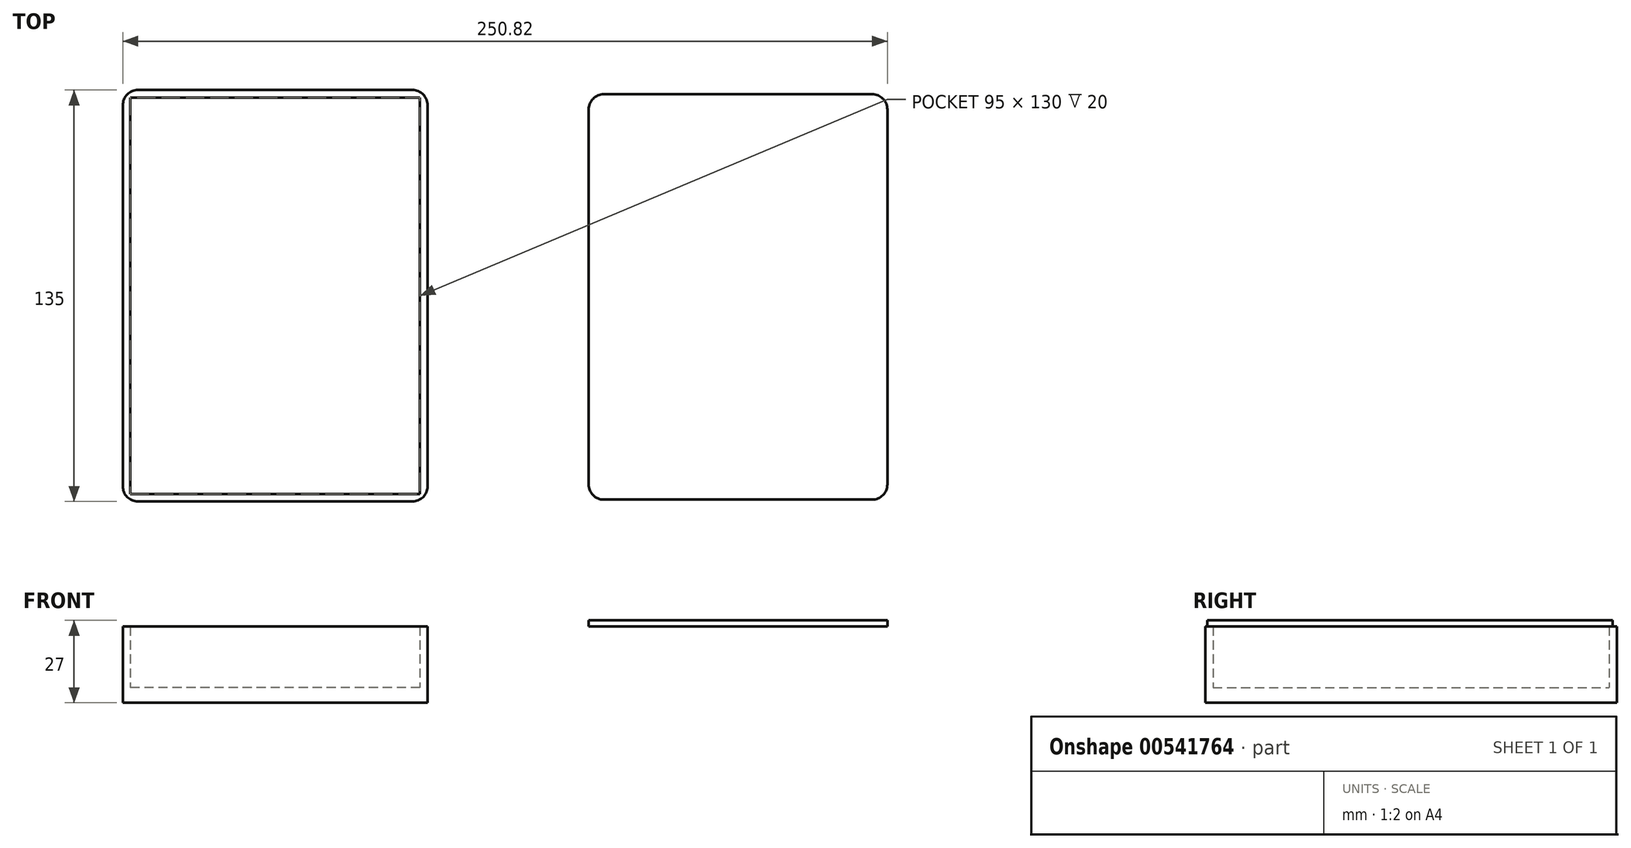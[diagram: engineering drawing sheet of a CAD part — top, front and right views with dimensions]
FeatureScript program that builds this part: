
annotation { "Feature Type Name" : "Feature", "Feature Type Description" : "" }
export const myFeature = defineFeature(function(context is Context, id is Id, definition is map)
    precondition{}
    {
        {
            var Q0;
            Q0=qCreatedBy(makeId("Top.planeOp"),FACE);
            var sketch = newSketch(context, id + "F0", { "sketchPlane" : qUnion([Q0])});
            skLineSegment(sketch, "E0.bottom", {"start": v(-50, -67.5) * mm, "end": v(50, -67.5) * mm});
            skLineSegment(sketch, "E0.top", {"start": v(-50, 67.5) * mm, "end": v(50, 67.5) * mm});
            skLineSegment(sketch, "E0.left", {"start": v(-50, -67.5) * mm, "end": v(-50, 67.5) * mm});
            skLineSegment(sketch, "E0.right", {"start": v(50, -67.5) * mm, "end": v(50, 67.5) * mm});
            skPoint(sketch, "E0.middle", {"position": v(0, 0) * mm});
            skSolve(sketch);
        }
        {
            var Q0;
            Q0=makeQuery(id+"F0.imprint","IMPRINT",FACE,{"disambiguationData":[TD([[makeQuery(id+"F0.imprint","IMPRINT",EDGE,{"derivedFrom":sQuery(id+"F0.wireOp",EDGE,"E0.bottom")}),1.0]])]});
            extrude(context, id + "F1", {"entities" : qUnion([Q0]), "oppositeDirection" : true, "depth" : 5 * mm, "offsetDistance" : 25 * mm});
        }
        {
            var Q0;
            Q0=makeQuery(id+"F1.opExtrude","CAP_FACE",FACE,{"disambiguationData":[OSD([sQuery(id+"F0.wireOp",EDGE,"E0.bottom"),sQuery(id+"F0.wireOp",EDGE,"E0.top"),sQuery(id+"F0.wireOp",EDGE,"E0.left"),sQuery(id+"F0.wireOp",EDGE,"E0.right")])],"isStart":true});
            var sketch = newSketch(context, id + "F2", { "sketchPlane" : qUnion([Q0])});
            skLineSegment(sketch, "E1.bottom", {"start": v(47.5, -65) * mm, "end": v(-47.5, -65) * mm});
            skLineSegment(sketch, "E1.top", {"start": v(47.5, 65) * mm, "end": v(-47.5, 65) * mm});
            skLineSegment(sketch, "E1.left", {"start": v(47.5, -65) * mm, "end": v(47.5, 65) * mm});
            skLineSegment(sketch, "E1.right", {"start": v(-47.5, -65) * mm, "end": v(-47.5, 65) * mm});
            skPoint(sketch, "E1.middle", {"position": v(0, 0) * mm});
            skSolve(sketch);
        }
        {
            var Q0;
            Q0=makeQuery(id+"F2.imprint","IMPRINT",FACE,{"disambiguationData":[TD([[makeQuery(id+"F2.imprint","IMPRINT",EDGE,{"derivedFrom":sQuery(id+"F2.wireOp",EDGE,"E1.bottom")}),1.0]])]});
            extrude(context, id + "F3", {"entities" : qUnion([Q0]), "operationType" : NewBodyOperationType.ADD, "depth" : 20 * mm, "offsetDistance" : 25 * mm});
        }
        {
            var Q0;
            {var subQ0=sQuery(id+"F0.wireOp",EDGE,"E0.right");var subQ1=sQuery(id+"F0.wireOp",EDGE,"E0.bottom");Q0=makeQuery(id+"F3.boolean.opBoolean","MERGE",EDGE,{"derivedFrom":[makeQuery(id+"F1.opExtrude","SWEPT_EDGE",EDGE,{"disambiguationData":[OSD([subQ1,subQ0])]}),makeQuery(id+"F3.opExtrude","SWEPT_EDGE",EDGE,{"disambiguationData":[OSD([subQ1,subQ0])]})]});}
            var Q1;
            {var subQ0=sQuery(id+"F0.wireOp",EDGE,"E0.left");var subQ1=sQuery(id+"F0.wireOp",EDGE,"E0.bottom");Q1=makeQuery(id+"F3.boolean.opBoolean","MERGE",EDGE,{"derivedFrom":[makeQuery(id+"F1.opExtrude","SWEPT_EDGE",EDGE,{"disambiguationData":[OSD([subQ1,subQ0])]}),makeQuery(id+"F3.opExtrude","SWEPT_EDGE",EDGE,{"disambiguationData":[OSD([subQ1,subQ0])]})]});}
            var Q2;
            {var subQ0=sQuery(id+"F0.wireOp",EDGE,"E0.left");var subQ1=sQuery(id+"F0.wireOp",EDGE,"E0.top");Q2=makeQuery(id+"F3.boolean.opBoolean","MERGE",EDGE,{"derivedFrom":[makeQuery(id+"F1.opExtrude","SWEPT_EDGE",EDGE,{"disambiguationData":[OSD([subQ1,subQ0])]}),makeQuery(id+"F3.opExtrude","SWEPT_EDGE",EDGE,{"disambiguationData":[OSD([subQ1,subQ0])]})]});}
            var Q3;
            {var subQ0=sQuery(id+"F0.wireOp",EDGE,"E0.right");var subQ1=sQuery(id+"F0.wireOp",EDGE,"E0.top");Q3=makeQuery(id+"F3.boolean.opBoolean","MERGE",EDGE,{"derivedFrom":[makeQuery(id+"F1.opExtrude","SWEPT_EDGE",EDGE,{"disambiguationData":[OSD([subQ1,subQ0])]}),makeQuery(id+"F3.opExtrude","SWEPT_EDGE",EDGE,{"disambiguationData":[OSD([subQ1,subQ0])]})]});}
            fillet(context, id + "F4", {"entities" : qUnion([Q0, Q1, Q2, Q3]), "radius" : 5 * mm, "tangentPropagation" : true, "allowEdgeOverflow" : false});
        }
        {
            var Q0;
            Q0=makeQuery(id+"F3.opExtrude","CAP_FACE",FACE,{"disambiguationData":[OSD([sQuery(id+"F0.wireOp",EDGE,"E0.bottom"),sQuery(id+"F0.wireOp",EDGE,"E0.top"),sQuery(id+"F0.wireOp",EDGE,"E0.left"),sQuery(id+"F0.wireOp",EDGE,"E0.right"),sQuery(id+"F2.wireOp",EDGE,"E1.bottom"),sQuery(id+"F2.wireOp",EDGE,"E1.top"),sQuery(id+"F2.wireOp",EDGE,"E1.left"),sQuery(id+"F2.wireOp",EDGE,"E1.right")])],"isStart":false});
            var sketch = newSketch(context, id + "F5", { "sketchPlane" : qUnion([Q0])});
            skLineSegment(sketch, "E2.bottom", {"start": v(102.82, 66.1) * mm, "end": v(200.82, 66.1) * mm});
            skLineSegment(sketch, "E2.top", {"start": v(102.82, -66.9) * mm, "end": v(200.82, -66.9) * mm});
            skLineSegment(sketch, "E2.left", {"start": v(102.82, 66.1) * mm, "end": v(102.82, -66.9) * mm});
            skLineSegment(sketch, "E2.right", {"start": v(200.82, 66.1) * mm, "end": v(200.82, -66.9) * mm});
            skSolve(sketch);
        }
        {
            var Q0;
            Q0=makeQuery(id+"F5.imprint","IMPRINT",FACE,{"disambiguationData":[TD([[makeQuery(id+"F5.imprint","IMPRINT",EDGE,{"derivedFrom":sQuery(id+"F5.wireOp",EDGE,"E2.bottom")}),-1.0]])]});
            extrude(context, id + "F6", {"entities" : qUnion([Q0]), "depth" : 2 * mm, "offsetDistance" : 25 * mm});
        }
        {
            var Q0;
            Q0=makeQuery(id+"F6.opExtrude","SWEPT_EDGE",EDGE,{"disambiguationData":[OSD([sQuery(id+"F5.wireOp",EDGE,"E2.top"),sQuery(id+"F5.wireOp",EDGE,"E2.left")])]});
            var Q1;
            Q1=makeQuery(id+"F6.opExtrude","SWEPT_EDGE",EDGE,{"disambiguationData":[OSD([sQuery(id+"F5.wireOp",EDGE,"E2.top"),sQuery(id+"F5.wireOp",EDGE,"E2.right")])]});
            var Q2;
            Q2=makeQuery(id+"F6.opExtrude","SWEPT_EDGE",EDGE,{"disambiguationData":[OSD([sQuery(id+"F5.wireOp",EDGE,"E2.bottom"),sQuery(id+"F5.wireOp",EDGE,"E2.right")])]});
            var Q3;
            Q3=makeQuery(id+"F6.opExtrude","SWEPT_EDGE",EDGE,{"disambiguationData":[OSD([sQuery(id+"F5.wireOp",EDGE,"E2.bottom"),sQuery(id+"F5.wireOp",EDGE,"E2.left")])]});
            fillet(context, id + "F7", {"entities" : qUnion([Q0, Q1, Q2, Q3]), "radius" : 5 * mm, "tangentPropagation" : true, "allowEdgeOverflow" : false});
        }
    });
